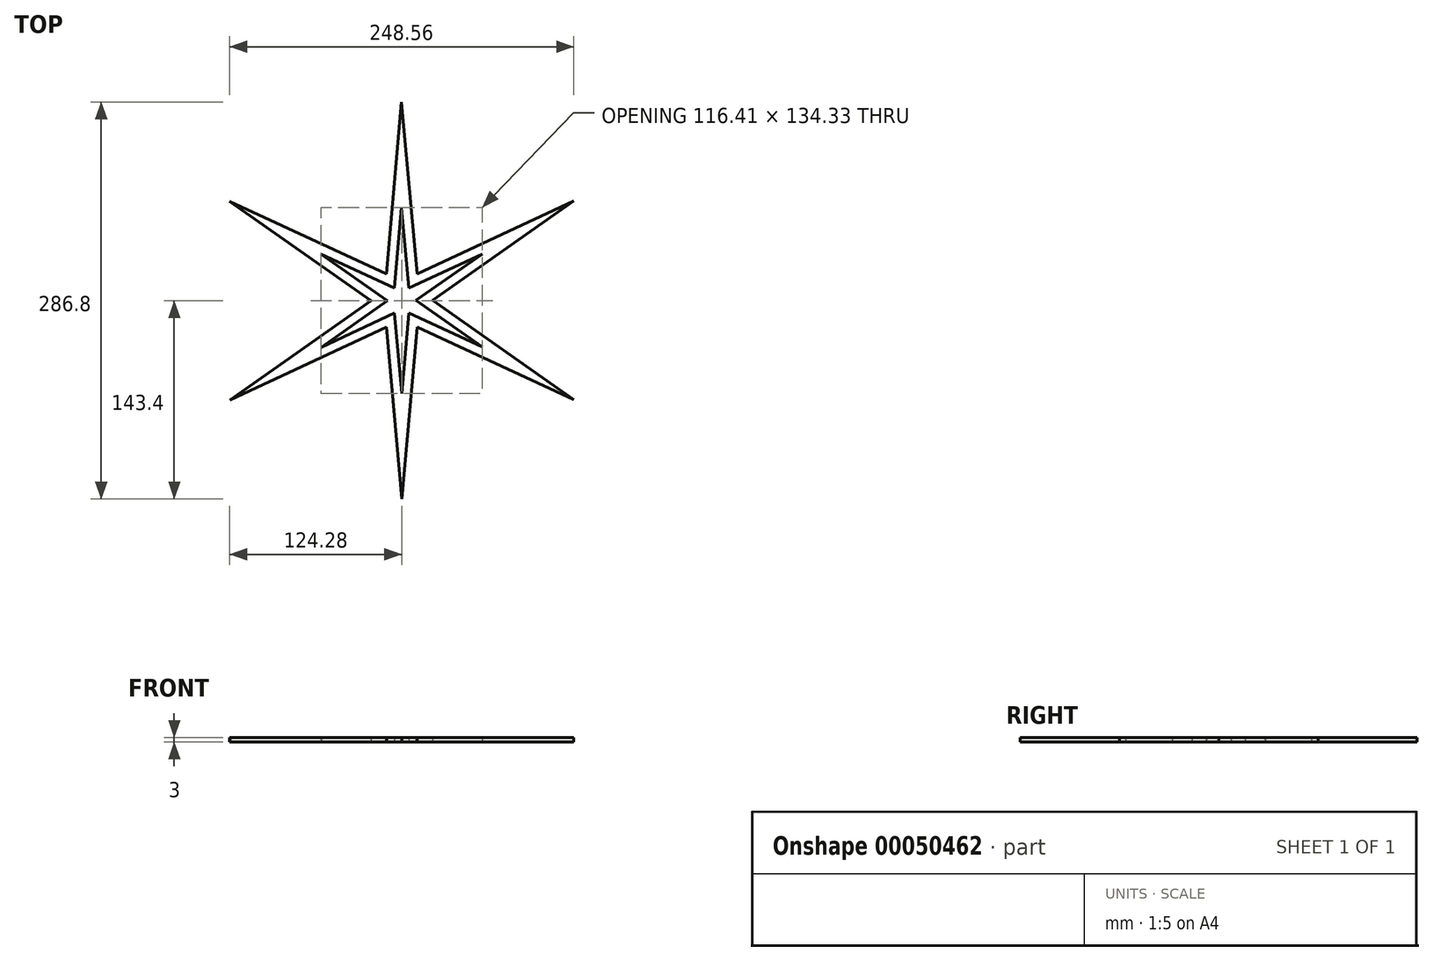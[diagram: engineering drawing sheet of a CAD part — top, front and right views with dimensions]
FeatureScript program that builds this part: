
annotation { "Feature Type Name" : "Feature", "Feature Type Description" : "" }
export const myFeature = defineFeature(function(context is Context, id is Id, definition is map)
    precondition{}
    {
        {
            var Q0;
            Q0=qCreatedBy(makeId("Top.planeOp"),FACE);
            var sketch = newSketch(context, id + "F0", { "sketchPlane" : qUnion([Q0])});
            skLineSegment(sketch, "E0", {"start": v(0, 0) * mm, "end": v(0.04, 0.07) * mm});
            skLineSegment(sketch, "E1", {"start": v(-58.2, 33.51) * mm, "end": v(-5.2, 9) * mm});
            skLineSegment(sketch, "E2", {"start": v(-5.2, 9) * mm, "end": v(-0.08, 67.16) * mm});
            skLineSegment(sketch, "E3.1.0", {"start": v(-58.12, -33.65) * mm, "end": v(-10.4, -0.01) * mm});
            skLineSegment(sketch, "E3.1.1", {"start": v(-10.4, -0.01) * mm, "end": v(-58.2, 33.51) * mm});
            skLineSegment(sketch, "E3.2.0", {"start": v(0.08, -67.16) * mm, "end": v(-5.19, -9.01) * mm});
            skLineSegment(sketch, "E3.2.1", {"start": v(-5.19, -9.01) * mm, "end": v(-58.12, -33.65) * mm});
            skLineSegment(sketch, "E3.3.0", {"start": v(58.2, -33.51) * mm, "end": v(5.2, -9) * mm});
            skLineSegment(sketch, "E3.3.1", {"start": v(5.2, -9) * mm, "end": v(0.08, -67.16) * mm});
            skLineSegment(sketch, "E3.4.0", {"start": v(58.12, 33.65) * mm, "end": v(10.4, 0.01) * mm});
            skLineSegment(sketch, "E3.4.1", {"start": v(10.4, 0.01) * mm, "end": v(58.2, -33.51) * mm});
            skLineSegment(sketch, "E3.5.0", {"start": v(-0.08, 67.16) * mm, "end": v(5.19, 9.01) * mm});
            skLineSegment(sketch, "E3.5.1", {"start": v(5.19, 9.01) * mm, "end": v(58.12, 33.65) * mm});
            skPoint(sketch, "E3.center", {"position": v(0, 0) * mm});
            skPoint(sketch, "E4.orphan", {"position": v(58.12, 33.65) * mm});
            skPoint(sketch, "E5.orphan", {"position": v(58.2, -33.51) * mm});
            skPoint(sketch, "E6.orphan", {"position": v(0.08, -67.16) * mm});
            skPoint(sketch, "E7.orphan", {"position": v(-58.12, -33.65) * mm});
            skLineSegment(sketch, "E8.0", {"start": v(11.12, -19.21) * mm, "end": v(0.17, -143.4) * mm});
            skLineSegment(sketch, "E8.1", {"start": v(-124.28, 71.55) * mm, "end": v(-11.12, 19.21) * mm});
            skLineSegment(sketch, "E8.2", {"start": v(-22.2, -0.03) * mm, "end": v(-124.28, 71.55) * mm});
            skLineSegment(sketch, "E8.3", {"start": v(-124.1, -71.85) * mm, "end": v(-22.2, -0.03) * mm});
            skLineSegment(sketch, "E8.4", {"start": v(-11.08, -19.24) * mm, "end": v(-124.1, -71.85) * mm});
            skLineSegment(sketch, "E8.5", {"start": v(-11.12, 19.21) * mm, "end": v(-0.17, 143.4) * mm});
            skLineSegment(sketch, "E8.6", {"start": v(0.17, -143.4) * mm, "end": v(-11.08, -19.24) * mm});
            skLineSegment(sketch, "E8.7", {"start": v(-0.17, 143.4) * mm, "end": v(11.08, 19.24) * mm});
            skLineSegment(sketch, "E8.8", {"start": v(11.08, 19.24) * mm, "end": v(124.1, 71.85) * mm});
            skLineSegment(sketch, "E8.9", {"start": v(124.1, 71.85) * mm, "end": v(22.2, 0.03) * mm});
            skLineSegment(sketch, "E8.10", {"start": v(22.2, 0.03) * mm, "end": v(124.28, -71.55) * mm});
            skLineSegment(sketch, "E8.11", {"start": v(124.28, -71.55) * mm, "end": v(11.12, -19.21) * mm});
            skCircle(sketch, "E9", {"center": v(0.04, 0.07) * mm, "radius": 5.93 * mm});
            skSolve(sketch);
        }
        {
            var Q0;
            Q0=makeQuery(id+"F0.imprint","IMPRINT",FACE,{"disambiguationData":[TD([[makeQuery(id+"F0.imprint","IMPRINT",EDGE,{"derivedFrom":sQuery(id+"F0.wireOp",EDGE,"E1")}),1.0]])]});
            extrude(context, id + "F1", {"entities" : qUnion([Q0]), "depth" : 3 * mm});
        }
    });
